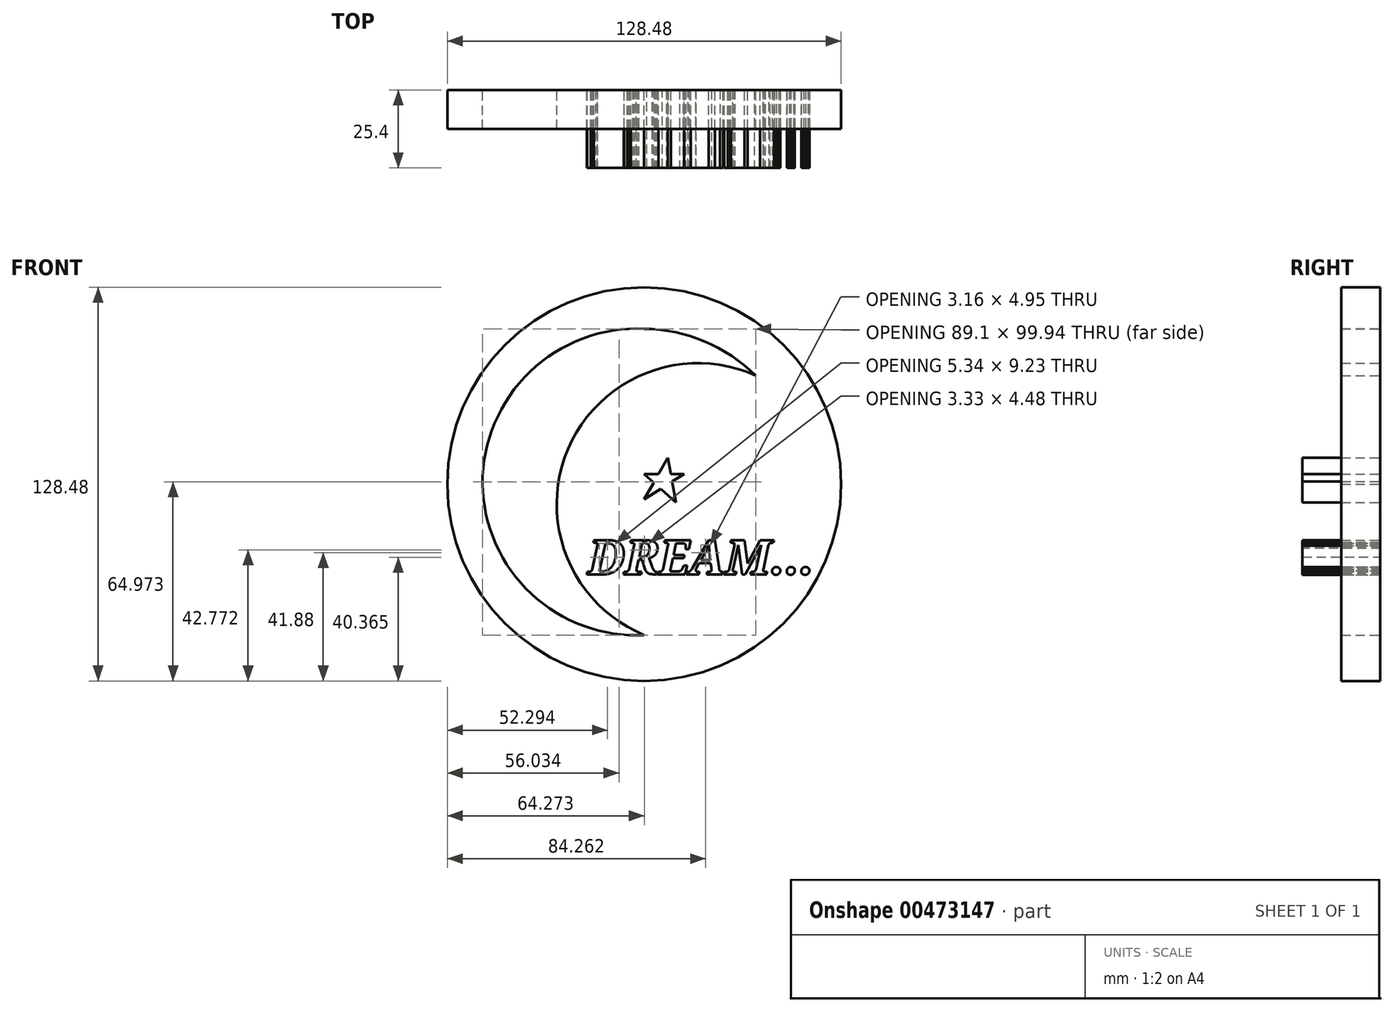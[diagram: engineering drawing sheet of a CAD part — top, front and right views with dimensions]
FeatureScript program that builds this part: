
annotation { "Feature Type Name" : "Feature", "Feature Type Description" : "" }
export const myFeature = defineFeature(function(context is Context, id is Id, definition is map)
    precondition{}
    {
        {
            var Q0;
            Q0=qCreatedBy(makeId("Front.planeOp"),FACE);
            var sketch = newSketch(context, id + "F0", { "sketchPlane" : qUnion([Q0])});
            skCircle(sketch, "E0", {"center": v(0, 0) * mm, "radius": 64.24 * mm});
            skPoint(sketch, "E1.orphan", {"position": v(0, 76.2) * mm});
            skPoint(sketch, "E2.start.orphan", {"position": v(-71.51, 65.06) * mm});
            skPoint(sketch, "E3.start.orphan", {"position": v(66.24, 65.06) * mm});
            skArc(sketch, "E4", {"start": v(0, 50.7) * mm, "mid": v(-37.26, 36.68) * mm, "end": v(-52.75, 0) * mm});
            skArc(sketch, "E5", {"start": v(-52.75, 0) * mm, "mid": v(-36.81, -35.8) * mm, "end": v(0, -49.24) * mm});
            skArc(sketch, "E6", {"start": v(36.34, 35.46) * mm, "mid": v(19.66, 46.63) * mm, "end": v(0, 50.7) * mm});
            skArc(sketch, "E7", {"start": v(36.34, 35.46) * mm, "mid": v(-24.82, 11.56) * mm, "end": v(0, -49.24) * mm});
            skSolve(sketch);
        }
        {
            var Q0;
            Q0=makeQuery(id+"F0.imprint","IMPRINT",FACE,{"disambiguationData":[TD([[makeQuery(id+"F0.imprint","IMPRINT",EDGE,{"derivedFrom":sQuery(id+"F0.wireOp",EDGE,"E0")}),1.0]])]});
            var sketch = newSketch(context, id + "F1", { "sketchPlane" : qUnion([Q0])});
            skLineSegment(sketch, "E8", {"start": v(7.72, 8.6) * mm, "end": v(4.7, 3.31) * mm});
            skLineSegment(sketch, "E9", {"start": v(0, -4.97) * mm, "end": v(5.4, -1.53) * mm});
            skLineSegment(sketch, "E10", {"start": v(13.01, 3.31) * mm, "end": v(8.68, 3.31) * mm});
            skLineSegment(sketch, "E11", {"start": v(0, 3.31) * mm, "end": v(3.12, 0.52) * mm});
            skLineSegment(sketch, "E12", {"start": v(10.36, -5.96) * mm, "end": v(9.13, 0.84) * mm});
            skLineSegment(sketch, "E13.trimOffspring", {"start": v(5.4, -1.53) * mm, "end": v(10.36, -5.96) * mm});
            skLineSegment(sketch, "E14.trimOffspring", {"start": v(3.12, 0.52) * mm, "end": v(0, -4.97) * mm});
            skLineSegment(sketch, "E15.trimOffspring", {"start": v(9.13, 0.84) * mm, "end": v(13.01, 3.31) * mm});
            skLineSegment(sketch, "E16.trimOffspring", {"start": v(8.68, 3.31) * mm, "end": v(7.72, 8.6) * mm});
            skLineSegment(sketch, "E17.trimOffspring", {"start": v(4.7, 3.31) * mm, "end": v(0, 3.31) * mm});
            skText(sketch, "E18", { "text": "DREAM...", "fontName": "NotoSerif-BoldItalic.ttf"});
            const initialGuessF1  = {"E18": [-0.01837, -0.02946, 1, 0, 0.01125]};
            skSetInitialGuess(sketch, initialGuessF1);
            skSolve(sketch);
        }
        {
            var Q0;
            Q0 = qSketchRegion(id + "F0", true);
            extrude(context, id + "F2", {"entities" : qUnion([Q0]), "depth" : 12.7 * mm});
        }
        {
            var Q0;
            Q0 = qSketchRegion(id + "F1", true);
            extrude(context, id + "F3", {"entities" : qUnion([Q0]), "depth" : 25.4 * mm});
        }
    });
